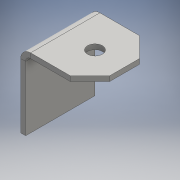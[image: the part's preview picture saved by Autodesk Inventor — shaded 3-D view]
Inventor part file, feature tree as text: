
AUTODESK INVENTOR PART (.ipt)
format: ipt  version: 2016 (Build 200138000, 138)  size: 108,544 bytes
history: native  units: in
note: dims shown in document units (in); Inventor stores cm internally (conversion verified against a paired STEP export)
features: other x3, sketch x3
ambient origin geometry x8: Origin, YZ Plane, XZ Plane, XY Plane, X Axis, Y Axis, Z Axis, Center Point
bodies: Solid1 (feature_tree)
feature tree (6):
  other  "Part120.ipt"
  other  "Solid1::Part120.ipt"
  other  "TaggingFeature1"
  sketch  "Sketch1"  dims[d0=0.3937in]
  sketch  "Sketch2"
  sketch  "Sketch3"
